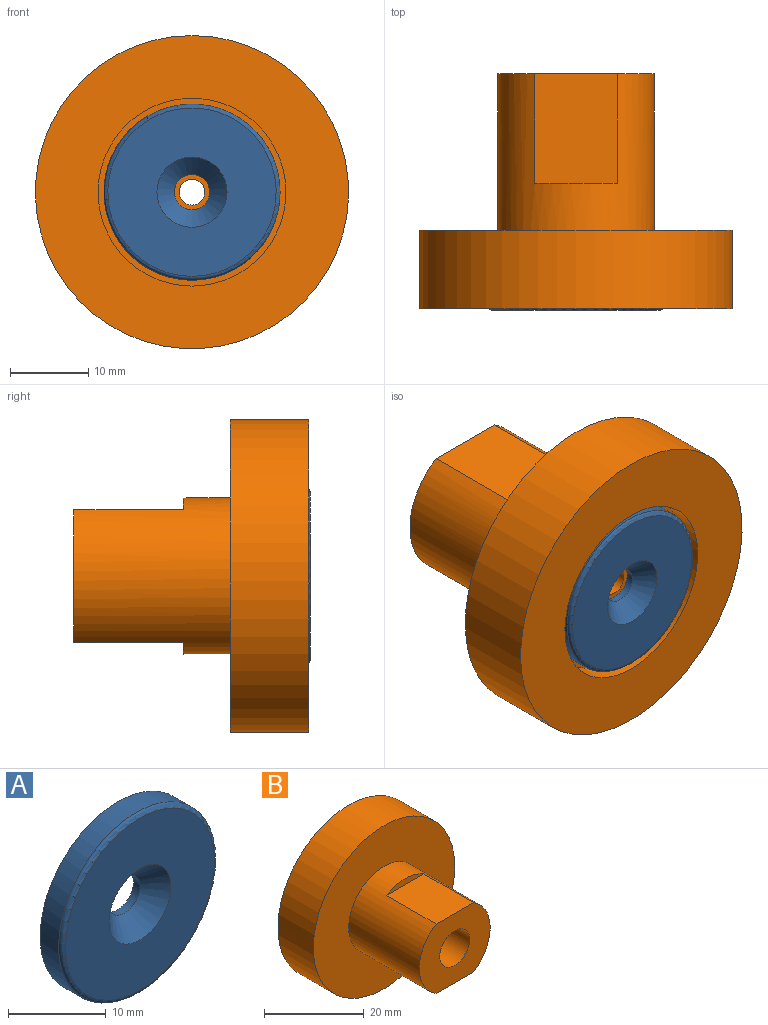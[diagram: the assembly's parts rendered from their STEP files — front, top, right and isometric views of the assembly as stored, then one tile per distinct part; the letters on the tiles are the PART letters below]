
ASSEMBLY  parts=2 mates=1
PART A: 6 faces, bbox 24.4x3.2x24.4 mm
  f0: cylinder r=11.25mm len=22.5mm, axis (0,1,0), area 189.1mm2, adj f2,f5
  f1: plane 21.5x21.5mm, normal (0,-1,0), area 300mm2, adj f4,f5
  f2: plane 22.5x22.5mm, normal (0,1,0), area 381.7mm2, adj f0,f3
  f3: cylinder r=2.25mm len=4.5mm, axis (0,-1,0), area 13.4mm2, adj f2,f4
  f4: cone r=2.25mm half-angle=45deg, axis (0,-1,0), area 66.7mm2, adj f1,f3
  f5: torus R=10.75mm, axis (0,-1,0), area 54.6mm2, adj f0,f1
PART B: 14 faces, bbox 40x30x40 mm
  f0: cylinder r=1.65mm len=7.44mm, axis (0,1,0), area 77.1mm2, adj f11,f12
  f1: cylinder r=10mm len=20mm, axis (0,1,0), area 945.9mm2, adj f2,f4,f6,f7,f8,f9
  f2: plane 20x17mm, normal (0,-1,0), area 236mm2, adj f1,f7,f9,f13
  f3: cylinder r=20mm len=40mm, axis (0,1,0), area 1256.6mm2, adj f4,f5
  f4: plane 40x40mm, normal (0,-1,0), area 942.5mm2, adj f1,f3
  f5: plane 40x40mm, normal (0,1,0), area 804.2mm2, adj f3,f10
  f6: plane 10.54x1.5mm, normal (0,-1,0), area 10.7mm2, adj f1,f7
  f7: plane 14x10.54mm, normal (0,0,1), area 147.5mm2, adj f1,f2,f6
  f8: plane 10.54x1.5mm, normal (0,-1,0), area 10.7mm2, adj f1,f9
  f9: plane 14x10.54mm, normal (0,0,-1), area 147.5mm2, adj f1,f2,f8
  f10: cylinder r=12mm len=24mm, axis (0,1,0), area 226.2mm2, adj f5,f11
  f11: plane 24x24mm, normal (0,1,0), area 443.8mm2, adj f0,f10
  f12: cone r=0mm half-angle=59deg, axis (0,-1,0), area 56.2mm2, adj f0,f13
  f13: cylinder r=4.25mm len=18mm, axis (0,-1,0), area 480.7mm2, adj f2,f12
PLACE A t=(-39.37,-18.84,3.46)mm
PLACE B rot(axis=(1,0,0),180deg) t=(-39.37,-21.84,3.46)mm
MATE fastened B.f10 <-> A.f0  axis (0,-1,0) through (-39.37,-18.84,3.46)mm
